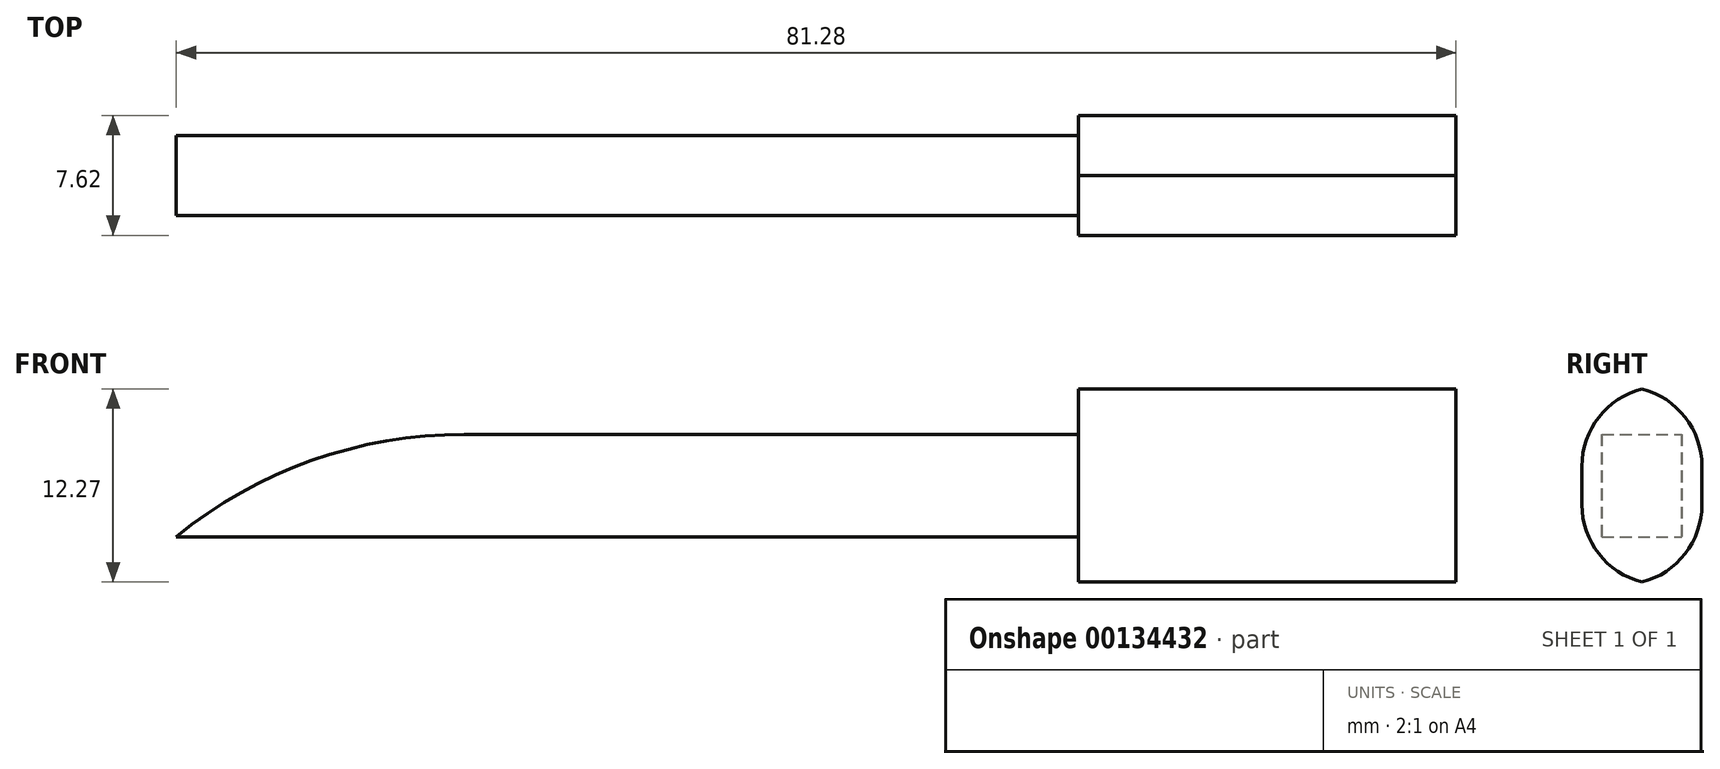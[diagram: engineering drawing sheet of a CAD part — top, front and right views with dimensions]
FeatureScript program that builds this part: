
annotation { "Feature Type Name" : "Feature", "Feature Type Description" : "" }
export const myFeature = defineFeature(function(context is Context, id is Id, definition is map)
    precondition{}
    {
        {
            var Q0;
            Q0=qCreatedBy(makeId("Front.planeOp"),FACE);
            var sketch = newSketch(context, id + "F0", { "sketchPlane" : qUnion([Q0])});
            skLineSegment(sketch, "E0", {"start": v(-55.13, 6.26) * mm, "end": v(2.17, 6.26) * mm});
            skLineSegment(sketch, "E1", {"start": v(2.17, 6.26) * mm, "end": v(2.17, 3.21) * mm});
            skLineSegment(sketch, "E2", {"start": v(2.17, 3.21) * mm, "end": v(26.15, 3.21) * mm});
            skLineSegment(sketch, "E3", {"start": v(26.15, 3.21) * mm, "end": v(26.15, 15.81) * mm});
            skLineSegment(sketch, "E4", {"start": v(26.15, 15.81) * mm, "end": v(2.17, 15.81) * mm});
            skLineSegment(sketch, "E5", {"start": v(2.17, 15.81) * mm, "end": v(2.17, 12.77) * mm});
            skLineSegment(sketch, "E6", {"start": v(2.17, 12.77) * mm, "end": v(-36.85, 12.77) * mm});
            skArc(sketch, "E7", {"start": v(-36.85, 12.77) * mm, "mid": v(-46.55, 11.1) * mm, "end": v(-55.13, 6.26) * mm});
            skLineSegment(sketch, "E8", {"start": v(2.17, 6.26) * mm, "end": v(2.17, 12.77) * mm});
            skLineSegment(sketch, "E9", {"start": v(26.15, 9.51) * mm, "end": v(2.17, 9.51) * mm});
            skSolve(sketch);
        }
        {
            var Q0;
            {var subQ1=sQuery(id+"F0.wireOp",EDGE,"E0");Q0=makeQuery(id+"F0.imprint","IMPRINT",FACE,{"disambiguationData":[TD([[makeQuery(id+"F0.imprint","IMPRINT",EDGE,{"derivedFrom":subQ1}),1.0]])]});}
            extrude(context, id + "F1", {"entities" : qUnion([Q0]), "endBound" : BoundingType.SYMMETRIC, "depth" : 5.08 * mm});
        }
        {
            var Q0;
            {var subQ1=sQuery(id+"F0.wireOp",EDGE,"E1");Q0=makeQuery(id+"F0.imprint","IMPRINT",FACE,{"disambiguationData":[TD([[makeQuery(id+"F0.imprint","IMPRINT",EDGE,{"derivedFrom":subQ1}),1.0]])]});}
            var Q1;
            {var subQ3=sQuery(id+"F0.wireOp",EDGE,"E4");Q1=makeQuery(id+"F0.imprint","IMPRINT",FACE,{"disambiguationData":[TD([[makeQuery(id+"F0.imprint","IMPRINT",EDGE,{"derivedFrom":subQ3}),1.0]])]});}
            extrude(context, id + "F2", {"entities" : qUnion([Q0, Q1]), "operationType" : NewBodyOperationType.ADD, "endBound" : BoundingType.SYMMETRIC, "depth" : 7.62 * mm});
        }
        {
            var Q0;
            Q0=makeQuery(id+"F2.opExtrude","CAP_EDGE",EDGE,{"disambiguationData":[OSD([sQuery(id+"F0.wireOp",EDGE,"E4")])],"isStart":false});
            var Q1;
            Q1=makeQuery(id+"F2.opExtrude","CAP_EDGE",EDGE,{"disambiguationData":[OSD([sQuery(id+"F0.wireOp",EDGE,"E2")])],"isStart":false});
            var Q2;
            Q2=makeQuery(id+"F2.opExtrude","CAP_EDGE",EDGE,{"disambiguationData":[OSD([sQuery(id+"F0.wireOp",EDGE,"E4")])],"isStart":true});
            var Q3;
            Q3=makeQuery(id+"F2.opExtrude","CAP_EDGE",EDGE,{"disambiguationData":[OSD([sQuery(id+"F0.wireOp",EDGE,"E2")])],"isStart":true});
            fillet(context, id + "F3", {"entities" : qUnion([Q0, Q1, Q2, Q3]), "radius" : 5.08 * mm, "tangentPropagation" : true, "allowEdgeOverflow" : false});
        }
    });
